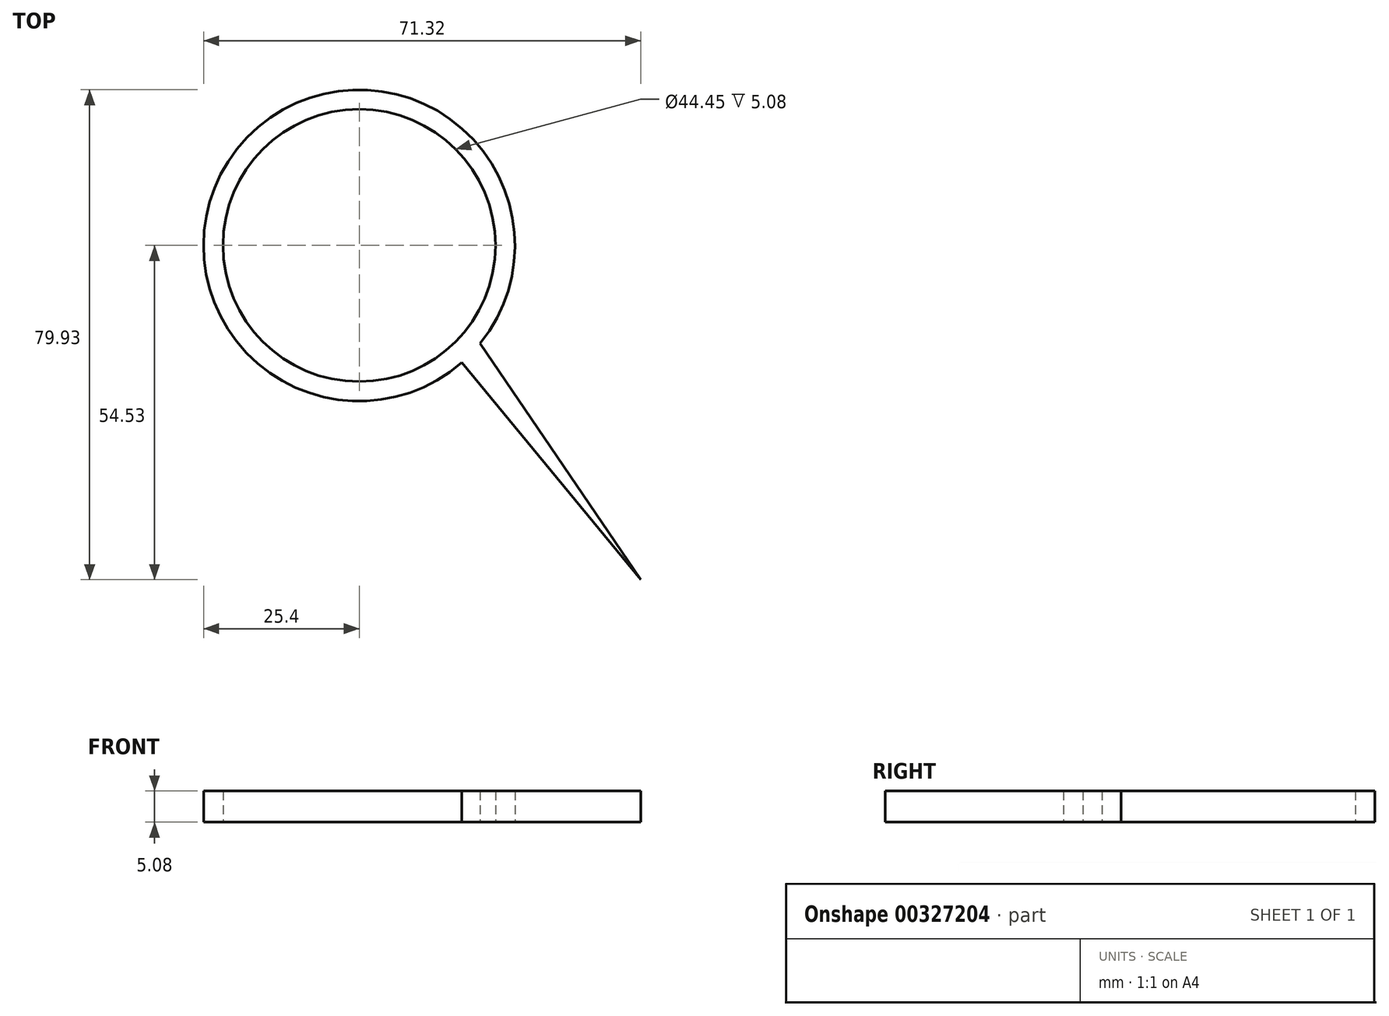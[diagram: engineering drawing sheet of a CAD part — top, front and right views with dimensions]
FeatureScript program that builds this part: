
annotation { "Feature Type Name" : "Feature", "Feature Type Description" : "" }
export const myFeature = defineFeature(function(context is Context, id is Id, definition is map)
    precondition{}
    {
        {
            var Q0;
            Q0=qCreatedBy(makeId("Top.planeOp"),FACE);
            var sketch = newSketch(context, id + "F0", { "sketchPlane" : qUnion([Q0])});
            skCircle(sketch, "E0", {"center": v(0, 0) * mm, "radius": 22.23 * mm});
            skArc(sketch, "E1", {"start": v(19.74, -15.99) * mm, "mid": v(-18.3, 17.6) * mm, "end": v(16.74, -19.1) * mm});
            skLineSegment(sketch, "E2", {"start": v(19.74, -15.99) * mm, "end": v(45.92, -54.53) * mm});
            skLineSegment(sketch, "E3", {"start": v(16.74, -19.1) * mm, "end": v(45.92, -54.53) * mm});
            skSolve(sketch);
        }
        {
            var Q0;
            Q0=makeQuery(id+"F0.imprint","IMPRINT",FACE,{"disambiguationData":[TD([[makeQuery(id+"F0.imprint","IMPRINT",EDGE,{"derivedFrom":sQuery(id+"F0.wireOp",EDGE,"E0")}),-1.0]])]});
            extrude(context, id + "F1", {"entities" : qUnion([Q0]), "depth" : 5.08 * mm});
        }
    });
